# Revit family: RPC Tree - Deciduous
name_source: partatom
category: Planting
revit_build: Autodesk Revit Architecture 2012 (Build: 20110210_1515)
units: mm (PartAtom-declared; Revit-internal decimal feet)

## types (18) — shared parameters
Assembly Code = G2050500

## per-type parameters (varying)
| type | Height | Type Comments |
| Red Ash - 25' | 25' - 0" | Red Maple |
| Fraxinus - 18' | 18' - 0" | Fraxinus |
| American Beech - 20' | 20' - 0" | American Beech |
| Blue Berry Elder - 15' | 15' - 0" | Blue Berry Elder |
| Common Apple - 20' | 20' - 0" | Common Apple |
| Golden Chain - 18' | 18' - 0" | Golden Chain |
| Gray Birch - 10' | 10' - 0" | Gray Birch |
| Hawthorn - 25' | 25' - 0" | Hawthorn |
| Honey Locust - 25' | 25' - 0" | Honey Locust |
| Japanese Cherry - 15' | 15' - 0" | Japanese Cherry |
| Japanese Maple - 10' | 10' - 0" | Japanese Maple |
| Kousa Dogwood - 10' | 10' - 0" | Kousa Dogwood |
| Largetooth Aspen - 25' | 25' - 0" | Largetooth Aspen |
| Lombardy Poplar - 40' | 40' - 0" | Lombardy Poplar |
| Red Maple - 30' | 30' - 0" | Red Maple |
| Scarlet Oak - 42' | 42' - 0" | Scarlet Oak |
| Schumard Oak - 30' | 30' - 0" | Schumard Oak |
| Siberian Crab Apple - 20' | 20' - 0" | Siberian Crab Apple |

## geometry (parser evidence)
native form markers: Sweep x1
no freeform markers — native parametric forms only
